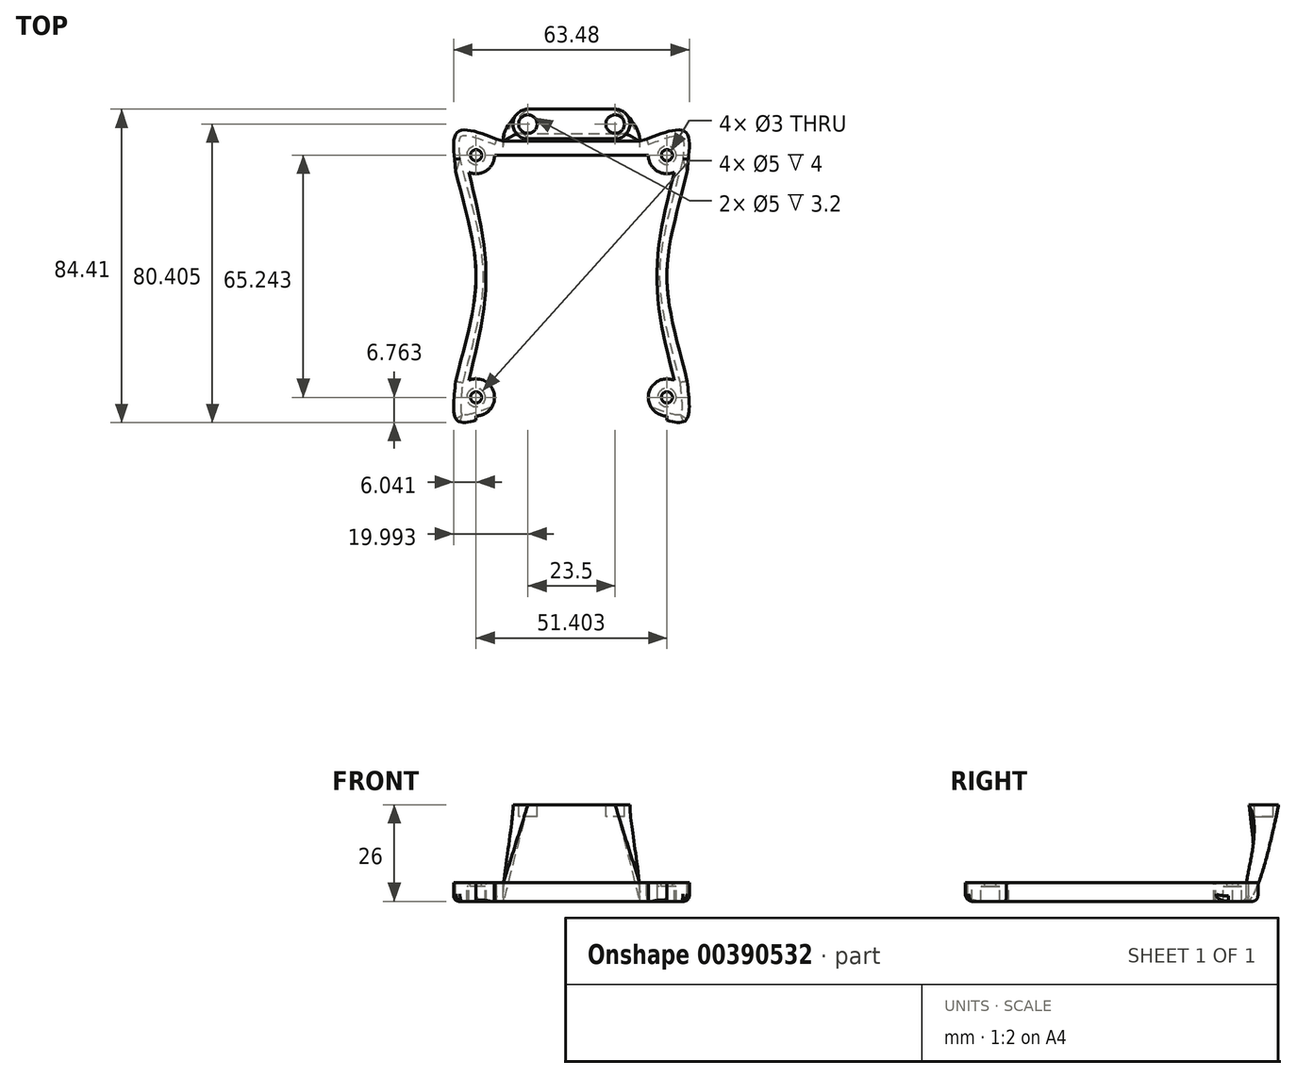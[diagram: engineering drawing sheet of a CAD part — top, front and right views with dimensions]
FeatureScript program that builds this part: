
annotation { "Feature Type Name" : "Feature", "Feature Type Description" : "" }
export const myFeature = defineFeature(function(context is Context, id is Id, definition is map)
    precondition{}
    {
        {
            var Q0;
            Q0=qCreatedBy(makeId("Top.planeOp"),FACE);
            var sketch = newSketch(context, id + "F0", { "sketchPlane" : qUnion([Q0])});
            skPoint(sketch, "E0.middle", {"position": v(-2.33, 0.15) * mm});
            skLineSegment(sketch, "E1.bottom", {"start": v(23.37, 32.78) * mm, "end": v(-28.03, 32.78) * mm, "construction": true});
            skLineSegment(sketch, "E1.top", {"start": v(23.37, -32.47) * mm, "end": v(-28.03, -32.47) * mm, "construction": true});
            skLineSegment(sketch, "E1.left", {"start": v(23.37, 32.78) * mm, "end": v(23.37, -32.47) * mm, "construction": true});
            skLineSegment(sketch, "E1.right", {"start": v(-28.03, 32.78) * mm, "end": v(-28.03, -32.47) * mm, "construction": true});
            skLineSegment(sketch, "E2.bottom", {"start": v(-67.33, 82.65) * mm, "end": v(62.67, 82.65) * mm, "construction": true});
            skLineSegment(sketch, "E2.top", {"start": v(-67.33, -82.35) * mm, "end": v(62.67, -82.35) * mm, "construction": true});
            skLineSegment(sketch, "E2.left", {"start": v(-67.33, 82.65) * mm, "end": v(-67.33, -82.35) * mm, "construction": true});
            skLineSegment(sketch, "E2.right", {"start": v(62.67, 82.65) * mm, "end": v(62.67, -82.35) * mm, "construction": true});
            skCircle(sketch, "E3", {"center": v(62.67, 82.65) * mm, "radius": 4.5 * mm, "construction": true});
            skCircle(sketch, "E4", {"center": v(-67.33, 82.65) * mm, "radius": 4.5 * mm, "construction": true});
            skCircle(sketch, "E5", {"center": v(62.67, -82.35) * mm, "radius": 4.5 * mm, "construction": true});
            skCircle(sketch, "E6", {"center": v(-67.33, -82.35) * mm, "radius": 4.5 * mm, "construction": true});
            skCircle(sketch, "E7", {"center": v(62.67, 82.65) * mm, "radius": 8 * mm, "construction": true});
            skCircle(sketch, "E8", {"center": v(62.67, -82.35) * mm, "radius": 8 * mm, "construction": true});
            skCircle(sketch, "E9", {"center": v(-67.33, -82.35) * mm, "radius": 8 * mm, "construction": true});
            skCircle(sketch, "E10", {"center": v(-67.33, 82.65) * mm, "radius": 8 * mm, "construction": true});
            skCircle(sketch, "E11", {"center": v(62.67, 82.65) * mm, "radius": 9.5 * mm, "construction": true});
            skCircle(sketch, "E12", {"center": v(62.67, -82.35) * mm, "radius": 9.5 * mm, "construction": true});
            skCircle(sketch, "E13", {"center": v(-67.33, -82.35) * mm, "radius": 9.5 * mm, "construction": true});
            skCircle(sketch, "E14", {"center": v(-67.33, 82.65) * mm, "radius": 9.5 * mm, "construction": true});
            skCircle(sketch, "E15", {"center": v(62.67, 82.65) * mm, "radius": 14 * mm, "construction": true});
            skCircle(sketch, "E16", {"center": v(-67.33, 82.65) * mm, "radius": 14 * mm, "construction": true});
            skCircle(sketch, "E17", {"center": v(62.67, -82.35) * mm, "radius": 14 * mm, "construction": true});
            skCircle(sketch, "E18", {"center": v(-67.33, -82.35) * mm, "radius": 14 * mm, "construction": true});
            skCircle(sketch, "E19", {"center": v(62.67, 82.65) * mm, "radius": 63.5 * mm, "construction": true});
            skCircle(sketch, "E20", {"center": v(62.67, -82.35) * mm, "radius": 63.5 * mm, "construction": true});
            skCircle(sketch, "E21", {"center": v(-67.33, -82.35) * mm, "radius": 63.5 * mm, "construction": true});
            skCircle(sketch, "E22", {"center": v(-67.33, 82.65) * mm, "radius": 63.5 * mm, "construction": true});
            skLineSegment(sketch, "E23.bottom", {"start": v(-28.52, 26.34) * mm, "end": v(23.86, 26.34) * mm, "construction": true});
            skLineSegment(sketch, "E23.top", {"start": v(-28.52, -26.04) * mm, "end": v(23.86, -26.04) * mm, "construction": true});
            skLineSegment(sketch, "E23.left", {"start": v(-28.52, 26.34) * mm, "end": v(-28.52, -26.04) * mm, "construction": true});
            skLineSegment(sketch, "E23.right", {"start": v(23.86, 26.34) * mm, "end": v(23.86, -26.04) * mm, "construction": true});
            skCircle(sketch, "E24", {"center": v(23.37, 32.78) * mm, "radius": 1.5 * mm, "construction": true});
            skCircle(sketch, "E25", {"center": v(-28.03, 32.78) * mm, "radius": 1.5 * mm, "construction": true});
            skCircle(sketch, "E26", {"center": v(23.37, -32.47) * mm, "radius": 1.5 * mm, "construction": true});
            skCircle(sketch, "E27", {"center": v(-28.03, -32.47) * mm, "radius": 1.5 * mm, "construction": true});
            skLineSegment(sketch, "E28", {"start": v(-67.33, 82.65) * mm, "end": v(62.67, -82.35) * mm, "construction": true});
            skLineSegment(sketch, "E29", {"start": v(62.67, 82.65) * mm, "end": v(-67.33, -82.35) * mm, "construction": true});
            skLineSegment(sketch, "E30.bottom", {"start": v(-17.58, -3.46) * mm, "end": v(12.92, -3.46) * mm, "construction": true});
            skLineSegment(sketch, "E30.top", {"start": v(-17.58, -33.96) * mm, "end": v(12.92, -33.96) * mm, "construction": true});
            skLineSegment(sketch, "E30.left", {"start": v(-17.58, -3.46) * mm, "end": v(-17.58, -33.96) * mm, "construction": true});
            skLineSegment(sketch, "E30.right", {"start": v(12.92, -3.46) * mm, "end": v(12.92, -33.96) * mm, "construction": true});
            skPoint(sketch, "E30.middle", {"position": v(-2.33, -18.71) * mm});
            skLineSegment(sketch, "E31.bottom", {"start": v(-17.58, 33.04) * mm, "end": v(12.92, 33.04) * mm, "construction": true});
            skLineSegment(sketch, "E31.top", {"start": v(-17.58, 2.54) * mm, "end": v(12.92, 2.54) * mm, "construction": true});
            skLineSegment(sketch, "E31.left", {"start": v(-17.58, 33.04) * mm, "end": v(-17.58, 2.54) * mm, "construction": true});
            skLineSegment(sketch, "E31.right", {"start": v(12.92, 33.04) * mm, "end": v(12.92, 2.54) * mm, "construction": true});
            skPoint(sketch, "E31.middle", {"position": v(-2.33, 17.79) * mm});
            skLineSegment(sketch, "E32", {"start": v(-2.33, 2.54) * mm, "end": v(-2.33, -3.46) * mm, "construction": true});
            skLineSegment(sketch, "E33", {"start": v(-2.33, 41.17) * mm, "end": v(-14.08, 41.17) * mm, "construction": true});
            skLineSegment(sketch, "E34", {"start": v(-2.33, 41.17) * mm, "end": v(9.42, 41.17) * mm, "construction": true});
            skLineSegment(sketch, "E35", {"start": v(-28.03, 32.78) * mm, "end": v(-22.53, 37.1) * mm, "construction": true});
            skLineSegment(sketch, "E36", {"start": v(-28.03, 32.78) * mm, "end": v(-33.53, 28.44) * mm, "construction": true});
            skLineSegment(sketch, "E37", {"start": v(-28.03, 32.78) * mm, "end": v(-32.98, 39.06) * mm, "construction": true});
            skLineSegment(sketch, "E38", {"start": v(23.37, 32.78) * mm, "end": v(28.33, 39.06) * mm, "construction": true});
            skLineSegment(sketch, "E39", {"start": v(23.37, 32.78) * mm, "end": v(17.88, 37.1) * mm, "construction": true});
            skLineSegment(sketch, "E40", {"start": v(23.37, 32.78) * mm, "end": v(28.87, 28.44) * mm, "construction": true});
            skLineSegment(sketch, "E41", {"start": v(23.37, -32.47) * mm, "end": v(28.33, -38.75) * mm, "construction": true});
            skLineSegment(sketch, "E42", {"start": v(23.37, -32.47) * mm, "end": v(17.88, -36.8) * mm, "construction": true});
            skLineSegment(sketch, "E43", {"start": v(23.37, -32.47) * mm, "end": v(28.87, -28.13) * mm, "construction": true});
            skLineSegment(sketch, "E44", {"start": v(-28.03, -32.47) * mm, "end": v(-32.98, -38.75) * mm, "construction": true});
            skLineSegment(sketch, "E45", {"start": v(-28.03, -32.47) * mm, "end": v(-22.53, -36.8) * mm, "construction": true});
            skLineSegment(sketch, "E46", {"start": v(-28.03, -32.47) * mm, "end": v(-33.53, -28.13) * mm, "construction": true});
            skFitSpline(sketch, "E47", {"points": [v(-22.53, 37.1) * mm, v(-32.98, 39.06) * mm, v(-33.53, 28.44) * mm], "startDerivative": vector(-20.3, 7.46) * mm, "endDerivative": vector(0.93, -21.61) * mm});
            skFitSpline(sketch, "E48", {"points": [v(17.88, 37.1) * mm, v(28.33, 39.06) * mm, v(28.87, 28.44) * mm], "startDerivative": vector(20.3, 7.46) * mm, "endDerivative": vector(-0.93, -21.61) * mm});
            skLineSegment(sketch, "E49", {"start": v(-14.08, 41.17) * mm, "end": v(-18.08, 41.17) * mm, "construction": true});
            skLineSegment(sketch, "E50", {"start": v(9.42, 41.17) * mm, "end": v(13.42, 41.17) * mm, "construction": true});
            skLineSegment(sketch, "E51", {"start": v(-2.33, 41.17) * mm, "end": v(-2.33, 45.17) * mm, "construction": true});
            skLineSegment(sketch, "E52", {"start": v(-18.08, 41.17) * mm, "end": v(-18.08, 41.17) * mm});
            skLineSegment(sketch, "E53", {"start": v(13.42, 41.17) * mm, "end": v(13.42, 41.17) * mm});
            skPoint(sketch, "E54.visualSharp", {"position": v(-18.08, 45.17) * mm});
            skPoint(sketch, "E55.visualSharp", {"position": v(13.42, 45.17) * mm});
            skLineSegment(sketch, "E56", {"start": v(-22.53, 37.1) * mm, "end": v(-20.66, 36.53) * mm});
            skPoint(sketch, "E57.visualSharp", {"position": v(-18.08, 35.74) * mm});
            skLineSegment(sketch, "E58", {"start": v(-18.08, 35.74) * mm, "end": v(-2.33, 35.74) * mm, "construction": true});
            skLineSegment(sketch, "E59", {"start": v(-2.33, 35.74) * mm, "end": v(13.42, 35.74) * mm, "construction": true});
            skLineSegment(sketch, "E60", {"start": v(17.88, 37.1) * mm, "end": v(16.01, 36.53) * mm});
            skPoint(sketch, "E61.visualSharp", {"position": v(13.42, 35.74) * mm});
            skCircle(sketch, "E62", {"center": v(-17.58, -33.96) * mm, "radius": 1.5 * mm});
            skCircle(sketch, "E63", {"center": v(12.92, -33.96) * mm, "radius": 1.5 * mm});
            skLineSegment(sketch, "E64", {"start": v(-2.33, -33.96) * mm, "end": v(-2.33, -37.96) * mm, "construction": true});
            skLineSegment(sketch, "E65", {"start": v(-17.58, -33.96) * mm, "end": v(-21.58, -33.96) * mm, "construction": true});
            skLineSegment(sketch, "E66", {"start": v(12.92, -33.96) * mm, "end": v(16.92, -33.96) * mm, "construction": true});
            skLineSegment(sketch, "E67", {"start": v(-21.58, -38.3) * mm, "end": v(-2.33, -38.3) * mm, "construction": true});
            skLineSegment(sketch, "E68", {"start": v(-2.33, -38.3) * mm, "end": v(16.92, -38.3) * mm, "construction": true});
            skPoint(sketch, "E69.visualSharp", {"position": v(-21.58, -38.3) * mm});
            skPoint(sketch, "E70.visualSharp", {"position": v(16.92, -38.3) * mm});
            skCircle(sketch, "E71", {"center": v(-12.13, -44.75) * mm, "radius": 1.5 * mm});
            skCircle(sketch, "E72", {"center": v(7.47, -44.75) * mm, "radius": 1.5 * mm});
            skLineSegment(sketch, "E73", {"start": v(-12.13, -44.75) * mm, "end": v(-2.33, -44.75) * mm, "construction": true});
            skLineSegment(sketch, "E74", {"start": v(-2.33, -44.75) * mm, "end": v(7.47, -44.75) * mm, "construction": true});
            skFitSpline(sketch, "E75", {"points": [v(-33.53, 28.44) * mm, v(-28.03, 0.15) * mm, v(-33.53, -28.13) * mm], "startDerivative": vector(16.96, -67.18) * mm, "endDerivative": vector(-16.96, -67.18) * mm});
            skFitSpline(sketch, "E76", {"points": [v(28.87, 28.44) * mm, v(23.37, 0.15) * mm, v(28.87, -28.13) * mm], "startDerivative": vector(-16.96, -67.18) * mm, "endDerivative": vector(16.96, -67.18) * mm});
            skLineSegment(sketch, "E77", {"start": v(-2.33, -44.75) * mm, "end": v(-2.33, -50.75) * mm, "construction": true});
            skLineSegment(sketch, "E78", {"start": v(-12.13, -44.75) * mm, "end": v(-16.13, -44.75) * mm, "construction": true});
            skLineSegment(sketch, "E79", {"start": v(-12.13, -44.75) * mm, "end": v(-12.13, -48.75) * mm, "construction": true});
            skLineSegment(sketch, "E80", {"start": v(7.47, -44.75) * mm, "end": v(11.47, -44.75) * mm, "construction": true});
            skLineSegment(sketch, "E81", {"start": v(7.47, -44.75) * mm, "end": v(7.47, -48.75) * mm, "construction": true});
            skCircle(sketch, "E82", {"center": v(-28.03, 32.78) * mm, "radius": 1.5 * mm});
            skCircle(sketch, "E83", {"center": v(23.37, 32.78) * mm, "radius": 1.5 * mm});
            skCircle(sketch, "E84", {"center": v(-28.03, -32.47) * mm, "radius": 1.5 * mm});
            skCircle(sketch, "E85", {"center": v(23.37, -32.47) * mm, "radius": 1.5 * mm});
            skLineSegment(sketch, "E86", {"start": v(-2.33, 32.78) * mm, "end": v(-2.33, 41.17) * mm, "construction": true});
            skLineSegment(sketch, "E87", {"start": v(115.22, -24.48) * mm, "end": v(115.22, 9.49) * mm, "construction": true});
            skLineSegment(sketch, "E88", {"start": v(-21.37, -36.36) * mm, "end": v(-2.33, -36.36) * mm, "construction": true});
            skLineSegment(sketch, "E89", {"start": v(-2.33, -36.36) * mm, "end": v(16.72, -36.36) * mm, "construction": true});
            skFitSpline(sketch, "E90", {"points": [v(-21.58, -38.3) * mm, v(-16.13, -44.75) * mm, v(-12.13, -48.75) * mm, v(-2.33, -50.75) * mm], "startDerivative": vector(17.01, -18.5) * mm, "endDerivative": vector(29.8, -3.11) * mm});
            skFitSpline(sketch, "E91", {"points": [v(16.92, -38.3) * mm, v(11.47, -44.75) * mm, v(7.47, -48.75) * mm, v(-2.33, -50.75) * mm], "startDerivative": vector(-17.98, -19.6) * mm, "endDerivative": vector(-29.8, -3.11) * mm});
            skLineSegment(sketch, "E92", {"start": v(116.25, 10.49) * mm, "end": v(169.47, 8.84) * mm, "construction": true});
            skPoint(sketch, "E93.visualSharp", {"position": v(115.22, 10.52) * mm});
            skArc(sketch, "E93.filletArc", {"start": v(116.25, 10.49) * mm, "mid": v(115.53, 10.2) * mm, "end": v(115.22, 9.49) * mm, "construction": true});
            skPoint(sketch, "E94.visualSharp", {"position": v(16.72, -36.36) * mm});
            skPoint(sketch, "E95.visualSharp", {"position": v(-21.37, -36.36) * mm});
            skLineSegment(sketch, "E96.bottom", {"start": v(-16.1, 17.65) * mm, "end": v(11.45, 17.65) * mm, "construction": true});
            skLineSegment(sketch, "E96.top", {"start": v(-16.1, -17.35) * mm, "end": v(11.45, -17.35) * mm, "construction": true});
            skLineSegment(sketch, "E96.left", {"start": v(-16.1, 17.65) * mm, "end": v(-16.1, -17.35) * mm, "construction": true});
            skLineSegment(sketch, "E96.right", {"start": v(11.45, 17.65) * mm, "end": v(11.45, -17.35) * mm, "construction": true});
            skLineSegment(sketch, "E97", {"start": v(-2.33, 13.23) * mm, "end": v(-20.53, 13.23) * mm, "construction": true});
            skLineSegment(sketch, "E98", {"start": v(-2.33, 13.23) * mm, "end": v(15.88, 13.23) * mm, "construction": true});
            skLineSegment(sketch, "E99", {"start": v(-2.33, 0.15) * mm, "end": v(-2.33, 14.42) * mm, "construction": true});
            skLineSegment(sketch, "E100", {"start": v(-2.33, 0.15) * mm, "end": v(14.67, 0.15) * mm, "construction": true});
            skLineSegment(sketch, "E101.bottom", {"start": v(-18.22, 14.7) * mm, "end": v(13.57, 14.7) * mm, "construction": true});
            skLineSegment(sketch, "E101.top", {"start": v(-18.22, -14.4) * mm, "end": v(13.57, -14.4) * mm, "construction": true});
            skLineSegment(sketch, "E101.left", {"start": v(-18.22, 14.7) * mm, "end": v(-18.22, -14.4) * mm, "construction": true});
            skLineSegment(sketch, "E101.right", {"start": v(13.57, 14.7) * mm, "end": v(13.57, -14.4) * mm, "construction": true});
            skLineSegment(sketch, "E102", {"start": v(-2.33, 26.07) * mm, "end": v(12, 26.07) * mm, "construction": true});
            skLineSegment(sketch, "E103", {"start": v(-2.33, 26.07) * mm, "end": v(-16.66, 26.07) * mm, "construction": true});
            skLineSegment(sketch, "E104.top", {"start": v(-17.4, 22.07) * mm, "end": v(-15.9, 22.07) * mm});
            skPoint(sketch, "E104.middle", {"position": v(-16.66, 26.07) * mm});
            skLineSegment(sketch, "E105.top", {"start": v(12.75, 22.07) * mm, "end": v(11.25, 22.07) * mm});
            skLineSegment(sketch, "E105.left", {"start": v(12.75, 30.07) * mm, "end": v(12.75, 22.07) * mm});
            skPoint(sketch, "E105.middle", {"position": v(12, 26.07) * mm});
            skFitSpline(sketch, "E106", {"points": [v(-33.53, -28.13) * mm, v(-32.98, -38.75) * mm, v(-22.93, -36.94) * mm], "startDerivative": vector(-1.92, -24.87) * mm, "endDerivative": vector(23.17, 7.34) * mm});
            skLineSegment(sketch, "E107", {"start": v(-22.93, -36.94) * mm, "end": v(-2.33, -36.94) * mm, "construction": true});
            skLineSegment(sketch, "E108", {"start": v(-2.33, -36.94) * mm, "end": v(18.28, -36.94) * mm, "construction": true});
            skLineSegment(sketch, "E109", {"start": v(16.92, -38.3) * mm, "end": v(17.66, -37.14) * mm});
            skLineSegment(sketch, "E110", {"start": v(18.25, -36.93) * mm, "end": v(18.28, -36.94) * mm});
            skLineSegment(sketch, "E111", {"start": v(-21.58, -38.3) * mm, "end": v(-22.32, -37.14) * mm});
            skLineSegment(sketch, "E112", {"start": v(-22.9, -36.93) * mm, "end": v(-22.93, -36.94) * mm});
            skLineSegment(sketch, "E113", {"start": v(169.47, 8.84) * mm, "end": v(169.47, -13.62) * mm, "construction": true});
            skPoint(sketch, "E114.visualSharp", {"position": v(17.88, -36.8) * mm});
            skArc(sketch, "E114.filletArc", {"start": v(18.25, -36.93) * mm, "mid": v(17.92, -36.93) * mm, "end": v(17.66, -37.14) * mm});
            skPoint(sketch, "E115.visualSharp", {"position": v(-22.53, -36.8) * mm});
            skArc(sketch, "E115.filletArc", {"start": v(-22.32, -37.14) * mm, "mid": v(-22.58, -36.93) * mm, "end": v(-22.9, -36.93) * mm});
            skLineSegment(sketch, "E116", {"start": v(-2.33, 0.15) * mm, "end": v(-2.33, 3.45) * mm, "construction": true});
            skLineSegment(sketch, "E117.bottom", {"start": v(-7.83, 5.65) * mm, "end": v(3.17, 5.65) * mm, "construction": true});
            skLineSegment(sketch, "E117.top", {"start": v(-7.83, -5.35) * mm, "end": v(3.17, -5.35) * mm, "construction": true});
            skLineSegment(sketch, "E117.left", {"start": v(-7.83, 5.65) * mm, "end": v(-7.83, -5.35) * mm, "construction": true});
            skLineSegment(sketch, "E117.right", {"start": v(3.17, 5.65) * mm, "end": v(3.17, -5.35) * mm, "construction": true});
            skLineSegment(sketch, "E118.bottom", {"start": v(-10.3, 10.77) * mm, "end": v(5.65, 10.77) * mm});
            skPoint(sketch, "E118.middle", {"position": v(-2.33, 12.75) * mm});
            skPoint(sketch, "E119.middle", {"position": v(-2.33, -26.45) * mm});
            skPoint(sketch, "E120", {"position": v(-2.33, -17.35) * mm});
            skPoint(sketch, "E121", {"position": v(-2.33, -26.04) * mm});
            skPoint(sketch, "E122.visualSharp", {"position": v(-2.33, 21.17) * mm});
            skArc(sketch, "E122.filletArc", {"start": v(-0.91, 19.76) * mm, "mid": v(-2.33, 20.34) * mm, "end": v(-3.74, 19.76) * mm});
            skPoint(sketch, "E123.visualSharp", {"position": v(-12.72, 10.77) * mm});
            skArc(sketch, "E123.filletArc", {"start": v(-11.02, 12.48) * mm, "mid": v(-11.23, 11.4) * mm, "end": v(-10.3, 10.77) * mm});
            skPoint(sketch, "E124.visualSharp", {"position": v(8.07, 10.77) * mm});
            skArc(sketch, "E124.filletArc", {"start": v(5.65, 10.77) * mm, "mid": v(6.58, 11.4) * mm, "end": v(6.36, 12.48) * mm});
            skPoint(sketch, "E125.visualSharp", {"position": v(-2.33, 0.75) * mm});
            skLineSegment(sketch, "E126", {"start": v(-1.33, 10.77) * mm, "end": v(-1.33, 6.27) * mm, "construction": true});
            skPoint(sketch, "E127.middle", {"position": v(-2.33, 9.75) * mm});
            skCircle(sketch, "E128", {"center": v(13.57, 14.7) * mm, "radius": 4.5 * mm, "construction": true});
            skCircle(sketch, "E129", {"center": v(-18.22, 14.7) * mm, "radius": 4.5 * mm, "construction": true});
            skCircle(sketch, "E130", {"center": v(13.57, -14.4) * mm, "radius": 4.5 * mm, "construction": true});
            skCircle(sketch, "E131", {"center": v(-18.22, -14.4) * mm, "radius": 4.5 * mm, "construction": true});
            skLineSegment(sketch, "E132", {"start": v(-2.33, 0.15) * mm, "end": v(-18.22, 14.7) * mm, "construction": true});
            skLineSegment(sketch, "E133", {"start": v(-2.33, 0.15) * mm, "end": v(13.57, 14.7) * mm, "construction": true});
            skLineSegment(sketch, "E134", {"start": v(13.57, 14.7) * mm, "end": v(23.37, 32.78) * mm, "construction": true});
            skLineSegment(sketch, "E135", {"start": v(-18.22, 14.7) * mm, "end": v(-28.03, 32.78) * mm, "construction": true});
            skLineSegment(sketch, "E136", {"start": v(-2.33, 0.15) * mm, "end": v(-18.22, -14.4) * mm, "construction": true});
            skLineSegment(sketch, "E137", {"start": v(-18.22, -14.4) * mm, "end": v(-28.03, -32.47) * mm, "construction": true});
            skLineSegment(sketch, "E138", {"start": v(-2.33, 0.15) * mm, "end": v(13.57, -14.4) * mm, "construction": true});
            skLineSegment(sketch, "E139", {"start": v(13.57, -14.4) * mm, "end": v(23.37, -32.47) * mm, "construction": true});
            skPoint(sketch, "E140.visualSharp", {"position": v(-4.57, 37.81) * mm});
            skPoint(sketch, "E141.visualSharp", {"position": v(-12.93, 29.46) * mm});
            skPoint(sketch, "E142.visualSharp", {"position": v(-4.57, 26.22) * mm});
            skArc(sketch, "E142.filletArc", {"start": v(-5.16, 25.63) * mm, "mid": v(-4.73, 26.28) * mm, "end": v(-4.57, 27.04) * mm});
            skPoint(sketch, "E143.visualSharp", {"position": v(-0.08, 26.22) * mm});
            skPoint(sketch, "E144.visualSharp", {"position": v(-0.08, 37.81) * mm});
            skPoint(sketch, "E145.visualSharp", {"position": v(8.28, 17.86) * mm});
            skPoint(sketch, "E146.visualSharp", {"position": v(-12.93, 17.86) * mm});
            skLineSegment(sketch, "E147", {"start": v(-2.33, -22.87) * mm, "end": v(-10.31, -22.87) * mm});
            skLineSegment(sketch, "E148", {"start": v(-2.33, -22.87) * mm, "end": v(5.66, -22.87) * mm});
            skPoint(sketch, "E149.visualSharp", {"position": v(8.07, -22.87) * mm});
            skArc(sketch, "E149.filletArc", {"start": v(6.37, -24.57) * mm, "mid": v(6.58, -23.48) * mm, "end": v(5.66, -22.87) * mm});
            skPoint(sketch, "E150.visualSharp", {"position": v(-12.73, -22.87) * mm});
            skArc(sketch, "E150.filletArc", {"start": v(-10.31, -22.87) * mm, "mid": v(-11.24, -23.48) * mm, "end": v(-11.02, -24.57) * mm});
            skPoint(sketch, "E151.visualSharp", {"position": v(-2.33, -33.27) * mm});
            skArc(sketch, "E151.filletArc", {"start": v(-3.74, -31.85) * mm, "mid": v(-2.33, -32.44) * mm, "end": v(-0.91, -31.85) * mm});
            skFitSpline(sketch, "E152", {"points": [v(28.87, -28.13) * mm, v(28.33, -38.75) * mm, v(18.28, -36.94) * mm], "startDerivative": vector(1.93, -24.89) * mm, "endDerivative": vector(-23.2, 7.39) * mm});
            skLineSegment(sketch, "E153", {"start": v(-5.66, -36.7) * mm, "end": v(-5.66, -42.34) * mm});
            skLineSegment(sketch, "E154", {"start": v(-12.73, -36.85) * mm, "end": v(-12.73, -31.22) * mm});
            skLineSegment(sketch, "E155", {"start": v(1, -36.7) * mm, "end": v(1, -42.34) * mm});
            skLineSegment(sketch, "E156", {"start": v(8.07, -36.85) * mm, "end": v(8.07, -31.22) * mm});
            skPoint(sketch, "E157.visualSharp", {"position": v(8.07, -28.8) * mm});
            skArc(sketch, "E157.filletArc", {"start": v(8.07, -31.22) * mm, "mid": v(7.46, -30.3) * mm, "end": v(6.37, -30.5) * mm});
            skPoint(sketch, "E158.visualSharp", {"position": v(1, -44.75) * mm});
            skArc(sketch, "E158.filletArc", {"start": v(1, -42.34) * mm, "mid": v(1.62, -43.26) * mm, "end": v(2.7, -43.05) * mm});
            skPoint(sketch, "E159.visualSharp", {"position": v(-5.66, -44.75) * mm});
            skArc(sketch, "E159.filletArc", {"start": v(-7.36, -43.05) * mm, "mid": v(-6.27, -43.26) * mm, "end": v(-5.66, -42.34) * mm});
            skPoint(sketch, "E160.visualSharp", {"position": v(-12.73, -28.8) * mm});
            skArc(sketch, "E160.filletArc", {"start": v(-11.02, -30.5) * mm, "mid": v(-12.1, -30.3) * mm, "end": v(-12.73, -31.22) * mm});
            skPoint(sketch, "E161.visualSharp", {"position": v(-5.66, -35.87) * mm});
            skArc(sketch, "E161.filletArc", {"start": v(-5.66, -36.7) * mm, "mid": v(-5.8, -35.94) * mm, "end": v(-6.24, -35.29) * mm});
            skPoint(sketch, "E162.visualSharp", {"position": v(-12.73, -37.68) * mm});
            skArc(sketch, "E162.filletArc", {"start": v(-12.73, -36.85) * mm, "mid": v(-12.57, -37.62) * mm, "end": v(-12.14, -38.27) * mm});
            skPoint(sketch, "E163.visualSharp", {"position": v(1, -35.87) * mm});
            skArc(sketch, "E163.filletArc", {"start": v(1.59, -35.29) * mm, "mid": v(1.15, -35.94) * mm, "end": v(1, -36.7) * mm});
            skPoint(sketch, "E164.visualSharp", {"position": v(8.07, -37.68) * mm});
            skArc(sketch, "E164.filletArc", {"start": v(7.49, -38.27) * mm, "mid": v(7.92, -37.62) * mm, "end": v(8.07, -36.85) * mm});
            skLineSegment(sketch, "E165", {"start": v(-2.33, -18.71) * mm, "end": v(-10.31, -18.71) * mm});
            skLineSegment(sketch, "E166", {"start": v(-2.33, -18.71) * mm, "end": v(5.66, -18.71) * mm});
            skPoint(sketch, "E167.visualSharp", {"position": v(-2.33, -8.31) * mm});
            skArc(sketch, "E167.filletArc", {"start": v(-0.91, -9.72) * mm, "mid": v(-2.33, -9.14) * mm, "end": v(-3.74, -9.72) * mm});
            skPoint(sketch, "E168.visualSharp", {"position": v(-12.73, -18.71) * mm});
            skArc(sketch, "E168.filletArc", {"start": v(-11.02, -17) * mm, "mid": v(-11.24, -18.1) * mm, "end": v(-10.31, -18.71) * mm});
            skPoint(sketch, "E169.visualSharp", {"position": v(8.07, -18.71) * mm});
            skArc(sketch, "E169.filletArc", {"start": v(5.66, -18.71) * mm, "mid": v(6.58, -18.1) * mm, "end": v(6.37, -17) * mm});
            skLineSegment(sketch, "E170", {"start": v(14.67, 0.15) * mm, "end": v(17.67, 0.15) * mm, "construction": true});
            skCircle(sketch, "E171", {"center": v(23.37, 32.78) * mm, "radius": 7 * mm, "construction": true});
            skLineSegment(sketch, "E172", {"start": v(17.64, 12.88) * mm, "end": v(21.69, 20.22) * mm});
            skLineSegment(sketch, "E173", {"start": v(16.8, 5.92) * mm, "end": v(12.23, 5.92) * mm});
            skPoint(sketch, "E174.visualSharp", {"position": v(22.7, 22.04) * mm});
            skArc(sketch, "E174.filletArc", {"start": v(22.15, 20.04) * mm, "mid": v(22, 20.33) * mm, "end": v(21.69, 20.22) * mm});
            skPoint(sketch, "E175.visualSharp", {"position": v(18.33, 5.92) * mm});
            skArc(sketch, "E175.filletArc", {"start": v(16.8, 5.92) * mm, "mid": v(18.02, 6.34) * mm, "end": v(18.73, 7.4) * mm});
            skPoint(sketch, "E176.visualSharp", {"position": v(9.29, 5.92) * mm});
            skArc(sketch, "E176.filletArc", {"start": v(11.62, 7.72) * mm, "mid": v(11.28, 6.6) * mm, "end": v(12.23, 5.92) * mm});
            skPoint(sketch, "E177.visualSharp", {"position": v(17.14, 11.97) * mm});
            skArc(sketch, "E177.filletArc", {"start": v(16.31, 11.33) * mm, "mid": v(17.06, 12.04) * mm, "end": v(17.64, 12.88) * mm});
            skLineSegment(sketch, "E178", {"start": v(9.29, 5.92) * mm, "end": v(-2.33, 5.92) * mm, "construction": true});
            skPoint(sketch, "E178.endSnap0", {"position": v(-2.33, 5.65) * mm});
            skLineSegment(sketch, "E179", {"start": v(-2.33, 5.92) * mm, "end": v(-13.94, 5.92) * mm, "construction": true});
            skLineSegment(sketch, "E180", {"start": v(-16.88, 5.92) * mm, "end": v(-21.46, 5.92) * mm});
            skLineSegment(sketch, "E181", {"start": v(17.14, 11.97) * mm, "end": v(-2.33, 11.97) * mm, "construction": true});
            skLineSegment(sketch, "E182", {"start": v(-2.33, 11.97) * mm, "end": v(-21.8, 11.97) * mm, "construction": true});
            skLineSegment(sketch, "E183", {"start": v(22.7, 22.04) * mm, "end": v(-2.33, 22.04) * mm, "construction": true});
            skLineSegment(sketch, "E184", {"start": v(-2.33, 22.04) * mm, "end": v(-27.34, 22.04) * mm, "construction": true});
            skLineSegment(sketch, "E185", {"start": v(-22.3, 12.88) * mm, "end": v(-26.34, 20.22) * mm});
            skPoint(sketch, "E186.visualSharp", {"position": v(-27.34, 22.04) * mm});
            skArc(sketch, "E186.filletArc", {"start": v(-26.34, 20.22) * mm, "mid": v(-26.65, 20.33) * mm, "end": v(-26.8, 20.04) * mm});
            skPoint(sketch, "E187.visualSharp", {"position": v(-13.94, 5.92) * mm});
            skArc(sketch, "E187.filletArc", {"start": v(-16.88, 5.92) * mm, "mid": v(-15.93, 6.6) * mm, "end": v(-16.27, 7.72) * mm});
            skPoint(sketch, "E188.visualSharp", {"position": v(-22.99, 5.92) * mm});
            skArc(sketch, "E188.filletArc", {"start": v(-23.39, 7.4) * mm, "mid": v(-22.67, 6.34) * mm, "end": v(-21.46, 5.92) * mm});
            skPoint(sketch, "E189.visualSharp", {"position": v(-21.8, 11.97) * mm});
            skArc(sketch, "E189.filletArc", {"start": v(-22.3, 12.88) * mm, "mid": v(-21.71, 12.04) * mm, "end": v(-20.97, 11.33) * mm});
            skLineSegment(sketch, "E190", {"start": v(-2.33, 43.17) * mm, "end": v(0, 43.17) * mm, "construction": true});
            skLineSegment(sketch, "E191", {"start": v(-20.66, 36.53) * mm, "end": v(16.01, 36.53) * mm});
            skSolve(sketch);
        }
        {
            var Q0;
            Q0=qCreatedBy(makeId("Top.planeOp"),FACE);
            cPlane(context, id + "F1", {"entities" : qUnion([Q0]), "cplaneType" : CPlaneType.OFFSET, "offset" : 21 * mm, "width" : 150 * mm, "height" : 150 * mm});
        }
        {
            var Q0;
            Q0=qCreatedBy(id+"F1.planeOp",FACE);
            var sketch = newSketch(context, id + "F2", { "sketchPlane" : qUnion([Q0])});
            skCircle(sketch, "E192", {"center": v(-14.08, 41.18) * mm, "radius": 4 * mm, "construction": true});
            skCircle(sketch, "E193", {"center": v(9.42, 41.18) * mm, "radius": 4 * mm, "construction": true});
            skLineSegment(sketch, "E194", {"start": v(-14.08, 41.18) * mm, "end": v(-14.08, 45.18) * mm, "construction": true});
            skLineSegment(sketch, "E195", {"start": v(-14.08, 41.18) * mm, "end": v(-18.08, 41.18) * mm, "construction": true});
            skLineSegment(sketch, "E196", {"start": v(9.42, 41.18) * mm, "end": v(9.42, 45.18) * mm, "construction": true});
            skLineSegment(sketch, "E197", {"start": v(9.42, 41.18) * mm, "end": v(13.42, 41.18) * mm, "construction": true});
            skArc(sketch, "E198", {"start": v(-14.08, 45.18) * mm, "mid": v(-16.9, 44) * mm, "end": v(-18.08, 41.18) * mm});
            skArc(sketch, "E199", {"start": v(13.42, 41.18) * mm, "mid": v(12.25, 44) * mm, "end": v(9.42, 45.18) * mm});
            skLineSegment(sketch, "E200", {"start": v(-14.08, 45.18) * mm, "end": v(9.42, 45.18) * mm});
            skLineSegment(sketch, "E201", {"start": v(-14.08, 41.18) * mm, "end": v(-14.08, 37.18) * mm, "construction": true});
            skLineSegment(sketch, "E202", {"start": v(9.42, 41.18) * mm, "end": v(9.42, 37.18) * mm, "construction": true});
            skArc(sketch, "E203", {"start": v(-18.08, 41.18) * mm, "mid": v(-16.9, 38.35) * mm, "end": v(-14.08, 37.18) * mm});
            skArc(sketch, "E204", {"start": v(9.42, 37.18) * mm, "mid": v(12.25, 38.35) * mm, "end": v(13.42, 41.18) * mm});
            skLineSegment(sketch, "E205", {"start": v(9.42, 37.18) * mm, "end": v(-14.08, 37.18) * mm});
            skLineSegment(sketch, "E206", {"start": v(-2.33, 37.18) * mm, "end": v(-2.33, 40.68) * mm, "construction": true});
            skLineSegment(sketch, "E207", {"start": v(-2.33, 40.68) * mm, "end": v(0, 40.68) * mm, "construction": true});
            skSolve(sketch);
        }
        {
            var Q0;
            Q0 = qSketchRegion(id + "F0", true);
            extrude(context, id + "F3", {"entities" : qUnion([Q0]), "oppositeDirection" : true, "depth" : 5 * mm});
        }
        {
            var Q0;
            Q0=sQuery(id+"F2.wireOp",VERTEX,"E200.start");
            var Q1;
            Q1=sQuery(id+"F2.wireOp",VERTEX,"E201.end");
            var Q2;
            Q2=makeQuery(id+"F3.opExtrude","CAP_VERTEX",VERTEX,{"disambiguationData":[OSD([sQuery(id+"F0.wireOp",EDGE,"E56"),sQuery(id+"F0.wireOp",EDGE,"E191")])],"isStart":true});
            cPlane(context, id + "F4", {"entities" : qUnion([Q0, Q1, Q2]), "cplaneType" : CPlaneType.THREE_POINT, "offset" : 25 * mm, "width" : 150 * mm, "height" : 150 * mm});
        }
        {
            var Q0;
            Q0=sQuery(id+"F2.wireOp",VERTEX,"E199.end");
            var Q1;
            Q1=sQuery(id+"F2.wireOp",VERTEX,"E205.start");
            var Q2;
            Q2=makeQuery(id+"F3.opExtrude","CAP_VERTEX",VERTEX,{"disambiguationData":[OSD([sQuery(id+"F0.wireOp",EDGE,"E60"),sQuery(id+"F0.wireOp",EDGE,"E191")])],"isStart":true});
            cPlane(context, id + "F5", {"entities" : qUnion([Q0, Q1, Q2]), "cplaneType" : CPlaneType.THREE_POINT, "offset" : 25 * mm, "width" : 150 * mm, "height" : 150 * mm});
        }
        {
            var Q0;
            Q0=qCreatedBy(id+"F4.planeOp",FACE);
            var sketch = newSketch(context, id + "F6", { "sketchPlane" : qUnion([Q0])});
            skFitSpline(sketch, "E208", {"points": [v(-37.18, 15.82) * mm, v(-36.53, -6.19) * mm], "startDerivative": vector(-8.46, -14.5) * mm, "endDerivative": vector(4.23, -21.62) * mm});
            skSolve(sketch);
        }
        {
            var Q0;
            Q0=sQuery(id+"F2.wireOp",VERTEX,"E200.start");
            var Q1;
            Q1=sQuery(id+"F6.wireOp",VERTEX,"E208.start");
            var Q2;
            Q2=makeQuery(id+"F3.opExtrude","CAP_VERTEX",VERTEX,{"disambiguationData":[OSD([sQuery(id+"F0.wireOp",EDGE,"E56"),sQuery(id+"F0.wireOp",EDGE,"E191")])],"isStart":false});
            cPlane(context, id + "F7", {"entities" : qUnion([Q0, Q1, Q2]), "cplaneType" : CPlaneType.THREE_POINT, "offset" : 25 * mm, "width" : 150 * mm, "height" : 150 * mm});
        }
        {
            var Q0;
            Q0=qCreatedBy(id+"F7.planeOp",FACE);
            var sketch = newSketch(context, id + "F8", { "sketchPlane" : qUnion([Q0])});
            skFitSpline(sketch, "E209", {"points": [v(-45.18, 16.9) * mm, v(-36.53, -9.92) * mm], "startDerivative": vector(1.94, -10.2) * mm, "endDerivative": vector(10.23, -0.3) * mm});
            skSolve(sketch);
        }
        {
            var Q0;
            Q0=qCreatedBy(id+"F5.planeOp",FACE);
            var sketch = newSketch(context, id + "F9", { "sketchPlane" : qUnion([Q0])});
            skFitSpline(sketch, "E210", {"points": [v(-37.18, 17.22) * mm, v(-36.53, -4.8) * mm], "startDerivative": vector(-9.48, -17.55) * mm, "endDerivative": vector(2.7, -19.83) * mm});
            skSolve(sketch);
        }
        {
            var Q0;
            Q0=sQuery(id+"F2.wireOp",VERTEX,"E199.end");
            var Q1;
            Q1=sQuery(id+"F9.wireOp",VERTEX,"E210.start");
            var Q2;
            Q2=makeQuery(id+"F3.opExtrude","CAP_VERTEX",VERTEX,{"disambiguationData":[OSD([sQuery(id+"F0.wireOp",EDGE,"E60"),sQuery(id+"F0.wireOp",EDGE,"E191")])],"isStart":false});
            cPlane(context, id + "F10", {"entities" : qUnion([Q0, Q1, Q2]), "cplaneType" : CPlaneType.THREE_POINT, "offset" : 25 * mm, "width" : 150 * mm, "height" : 150 * mm});
        }
        {
            var Q0;
            Q0=qCreatedBy(id+"F10.planeOp",FACE);
            var sketch = newSketch(context, id + "F11", { "sketchPlane" : qUnion([Q0])});
            skFitSpline(sketch, "E211", {"points": [v(-45.18, 18.04) * mm, v(-36.53, -8.78) * mm], "startDerivative": vector(1.66, -8.07) * mm, "endDerivative": vector(10.78, -0.87) * mm});
            skSolve(sketch);
        }
        {
            var Q1;
            Q1=makeQuery(id+"F2.imprint","IMPRINT",FACE,{"disambiguationData":[TD([[makeQuery(id+"F2.imprint","IMPRINT",EDGE,{"derivedFrom":sQuery(id+"F2.wireOp",EDGE,"E198")}),1.0]])]});
            var Q2;
            Q2=makeQuery(id+"F3.opExtrude","SWEPT_FACE",FACE,{"disambiguationData":[OSD([sQuery(id+"F0.wireOp",EDGE,"E191")])]});
            var Q3;
            Q3=sQuery(id+"F11.wireOp",EDGE,"E211");
            var Q4;
            Q4=sQuery(id+"F8.wireOp",EDGE,"E209");
            var Q5;
            Q5=sQuery(id+"F9.wireOp",EDGE,"E210");
            var Q6;
            Q6=sQuery(id+"F6.wireOp",EDGE,"E208");
            loft(context, id + "F12", {"operationType" : NewBodyOperationType.ADD, "addGuides" : true, "sheetProfilesArray" : [{ "sheetProfileEntities" : qUnion([Q1]) }, { "sheetProfileEntities" : qUnion([Q2]) }], "guidesArray" : [{ "guideEntities" : qUnion([Q3]), "guideDerivativeType" : LoftGuideDerivativeType.DEFAULT, "guideDerivativeMagnitude" : 1 }, { "guideEntities" : qUnion([Q4]), "guideDerivativeType" : LoftGuideDerivativeType.DEFAULT, "guideDerivativeMagnitude" : 1 }, { "guideEntities" : qUnion([Q5]), "guideDerivativeType" : LoftGuideDerivativeType.DEFAULT, "guideDerivativeMagnitude" : 1 }, { "guideEntities" : qUnion([Q6]), "guideDerivativeType" : LoftGuideDerivativeType.DEFAULT, "guideDerivativeMagnitude" : 1 }]});
        }
        {
            var Q0;
            Q0=qCreatedBy(makeId("Top.planeOp"),FACE);
            var sketch = newSketch(context, id + "F13", { "sketchPlane" : qUnion([Q0])});
            skLineSegment(sketch, "E212", {"start": v(0, 15.53) * mm, "end": v(-2.33, 15.53) * mm, "construction": true});
            skLineSegment(sketch, "E213", {"start": v(-2.33, 34.2) * mm, "end": v(-2.33, -48.18) * mm, "construction": true});
            skCircle(sketch, "E214", {"center": v(-28.03, 32.78) * mm, "radius": 5 * mm, "construction": true});
            skCircle(sketch, "E215", {"center": v(23.37, 32.78) * mm, "radius": 5 * mm, "construction": true});
            skLineSegment(sketch, "E216", {"start": v(-23.03, 32.78) * mm, "end": v(18.37, 32.78) * mm});
            skArc(sketch, "E217", {"start": v(-28.03, 27.78) * mm, "mid": v(-24.5, 29.24) * mm, "end": v(-23.03, 32.78) * mm});
            skArc(sketch, "E218", {"start": v(18.37, 32.78) * mm, "mid": v(19.84, 29.24) * mm, "end": v(23.37, 27.78) * mm});
            skCircle(sketch, "E219", {"center": v(-28.03, -32.47) * mm, "radius": 5 * mm, "construction": true});
            skCircle(sketch, "E220", {"center": v(23.37, -32.47) * mm, "radius": 5 * mm, "construction": true});
            skLineSegment(sketch, "E221", {"start": v(23.37, -37.47) * mm, "end": v(23.37, -52.19) * mm});
            skLineSegment(sketch, "E222", {"start": v(-2.33, 0) * mm, "end": v(-25.33, 0) * mm, "construction": true});
            skLineSegment(sketch, "E223", {"start": v(-2.33, 0) * mm, "end": v(20.67, 0) * mm, "construction": true});
            skArc(sketch, "E224", {"start": v(23.37, -27.47) * mm, "mid": v(18.37, -32.47) * mm, "end": v(23.37, -37.47) * mm});
            skLineSegment(sketch, "E225", {"start": v(-28.03, -37.47) * mm, "end": v(-28.03, -52.19) * mm});
            skLineSegment(sketch, "E226", {"start": v(-28.03, -52.19) * mm, "end": v(23.37, -52.19) * mm});
            skArc(sketch, "E227", {"start": v(-28.03, -37.47) * mm, "mid": v(-23.06, -32.47) * mm, "end": v(-28.03, -27.47) * mm});
            skLineSegment(sketch, "E228", {"start": v(-23.03, 32.78) * mm, "end": v(-30, 32.78) * mm, "construction": true});
            skLineSegment(sketch, "E229", {"start": v(18.37, 32.78) * mm, "end": v(25.35, 32.78) * mm, "construction": true});
            skLineSegment(sketch, "E230", {"start": v(-23.06, -32.47) * mm, "end": v(-30.03, -32.47) * mm, "construction": true});
            skLineSegment(sketch, "E231", {"start": v(18.37, -32.47) * mm, "end": v(25.35, -32.47) * mm, "construction": true});
            skPoint(sketch, "E231.startSnap0", {"position": v(18.37, -32.47) * mm});
            skFitSpline(sketch, "E232", {"points": [v(-30, 28.18) * mm, v(-25.33, 0) * mm, v(-30, -27.87) * mm], "startDerivative": vector(14.01, -56.3) * mm, "endDerivative": vector(-14.04, -55.82) * mm});
            skFitSpline(sketch, "E233", {"points": [v(25.35, 28.18) * mm, v(20.67, 0) * mm, v(25.35, -27.87) * mm], "startDerivative": vector(-14.01, -56.3) * mm, "endDerivative": vector(14.04, -55.82) * mm});
            skArc(sketch, "E234", {"start": v(-28.03, -27.47) * mm, "mid": v(-29.04, -27.57) * mm, "end": v(-30, -27.87) * mm});
            skArc(sketch, "E235", {"start": v(25.35, -27.87) * mm, "mid": v(24.38, -27.57) * mm, "end": v(23.37, -27.47) * mm});
            skArc(sketch, "E236", {"start": v(-30, 28.18) * mm, "mid": v(-29.04, 27.88) * mm, "end": v(-28.03, 27.78) * mm});
            skArc(sketch, "E237", {"start": v(23.37, 27.78) * mm, "mid": v(24.38, 27.88) * mm, "end": v(25.35, 28.18) * mm});
            skSolve(sketch);
        }
        {
            var Q0;
            Q0 = qSketchRegion(id + "F13", true);
            extrude(context, id + "F14", {"entities" : qUnion([Q0]), "operationType" : NewBodyOperationType.REMOVE, "oppositeDirection" : true, "depth" : 5 * mm});
        }
        {
            var Q0;
            Q0=makeQuery(id+"F3.opExtrude","CAP_EDGE",EDGE,{"disambiguationData":[OSD([sQuery(id+"F0.wireOp",EDGE,"E75")])],"isStart":false});
            var Q1;
            Q1=makeQuery(id+"F3.opExtrude","CAP_EDGE",EDGE,{"disambiguationData":[OSD([sQuery(id+"F0.wireOp",EDGE,"E76")])],"isStart":false});
            var Q2;
            Q2=makeQuery(id+"F14.boolean.opBoolean","COPY",EDGE,{"derivedFrom":makeQuery(id+"F14.opExtrude","CAP_EDGE",EDGE,{"disambiguationData":[OSD([sQuery(id+"F13.wireOp",EDGE,"3efa2638-28cb-410d-a451-7c4a5f4f91e7")])],"isStart":false})});
            var Q3;
            Q3=makeQuery(id+"F14.boolean.opBoolean","COPY",EDGE,{"derivedFrom":makeQuery(id+"F14.opExtrude","CAP_EDGE",EDGE,{"disambiguationData":[OSD([sQuery(id+"F13.wireOp",EDGE,"fab21a03-1c0a-4784-8c2c-017c8e7d5961")])],"isStart":false})});
            var Q4;
            Q4=makeQuery(id+"F3.opExtrude","CAP_EDGE",EDGE,{"disambiguationData":[OSD([sQuery(id+"F0.wireOp",EDGE,"E152")])],"isStart":false});
            var Q5;
            Q5=makeQuery(id+"F3.opExtrude","CAP_EDGE",EDGE,{"disambiguationData":[OSD([sQuery(id+"F0.wireOp",EDGE,"E106")])],"isStart":false});
            fillet(context, id + "F15", {"entities" : qUnion([Q0, Q1, Q2, Q3, Q4, Q5]), "radius" : 2 * mm, "tangentPropagation" : true, "allowEdgeOverflow" : false});
        }
        {
            var Q0;
            Q0=makeQuery(id+"F3.opExtrude","CAP_EDGE",EDGE,{"disambiguationData":[OSD([sQuery(id+"F0.wireOp",EDGE,"E47")])],"isStart":false});
            var Q1;
            Q1=makeQuery(id+"F3.opExtrude","CAP_EDGE",EDGE,{"disambiguationData":[OSD([sQuery(id+"F0.wireOp",EDGE,"E48")])],"isStart":false});
            fillet(context, id + "F16", {"entities" : qUnion([Q0, Q1]), "radius" : 1.5 * mm, "tangentPropagation" : true, "allowEdgeOverflow" : false});
        }
        {
            var Q0;
            Q0=qCreatedBy(makeId("Top.planeOp"),FACE);
            var sketch = newSketch(context, id + "F17", { "sketchPlane" : qUnion([Q0])});
            skCircle(sketch, "E238", {"center": v(-28.03, 32.78) * mm, "radius": 2.5 * mm});
            skCircle(sketch, "E239", {"center": v(23.37, 32.78) * mm, "radius": 2.5 * mm});
            skCircle(sketch, "E240", {"center": v(23.37, -32.47) * mm, "radius": 2.5 * mm});
            skCircle(sketch, "E241", {"center": v(-28.03, -32.47) * mm, "radius": 2.5 * mm});
            skSolve(sketch);
        }
        {
            var Q0;
            Q0 = qSketchRegion(id + "F17", true);
            extrude(context, id + "F18", {"entities" : qUnion([Q0]), "operationType" : NewBodyOperationType.REMOVE, "oppositeDirection" : true, "depth" : 5 * mm, "hasSecondDirection" : true, "secondDirectionOppositeDirection" : true, "secondDirectionDepth" : 1 * mm});
        }
        {
            var Q0;
            Q0=qCreatedBy(id+"F1.planeOp",FACE);
            var sketch = newSketch(context, id + "F19", { "sketchPlane" : qUnion([Q0])});
            skCircle(sketch, "E242", {"center": v(-14.08, 41.18) * mm, "radius": 1.5 * mm});
            skCircle(sketch, "E243", {"center": v(9.42, 41.18) * mm, "radius": 1.5 * mm});
            skCircle(sketch, "E244", {"center": v(-14.08, 41.18) * mm, "radius": 2.5 * mm});
            skCircle(sketch, "E245", {"center": v(9.42, 41.18) * mm, "radius": 2.5 * mm});
            skSolve(sketch);
        }
        {
            var Q0;
            Q0=qCreatedBy(id+"F1.planeOp",FACE);
            var sketch = newSketch(context, id + "F20", { "sketchPlane" : qUnion([Q0])});
            skArc(sketch, "E246", {"start": v(-16.58, 41.18) * mm, "mid": v(-14.08, 38.68) * mm, "end": v(-11.58, 41.18) * mm});
            skArc(sketch, "E247", {"start": v(6.92, 41.18) * mm, "mid": v(9.42, 38.68) * mm, "end": v(11.92, 41.18) * mm});
            skLineSegment(sketch, "E248", {"start": v(-16.58, 41.18) * mm, "end": v(-16.58, 45.78) * mm});
            skLineSegment(sketch, "E249", {"start": v(-11.58, 41.18) * mm, "end": v(-11.58, 45.78) * mm});
            skLineSegment(sketch, "E250", {"start": v(-11.58, 45.78) * mm, "end": v(-16.58, 45.78) * mm});
            skLineSegment(sketch, "E251", {"start": v(6.92, 41.18) * mm, "end": v(6.92, 46.07) * mm});
            skLineSegment(sketch, "E252", {"start": v(11.92, 41.18) * mm, "end": v(11.92, 46.07) * mm});
            skLineSegment(sketch, "E253", {"start": v(11.92, 46.07) * mm, "end": v(6.92, 46.07) * mm});
            skSolve(sketch);
        }
        {
            var Q0;
            Q0=qCreatedBy(id+"F1.planeOp",FACE);
            var sketch = newSketch(context, id + "F21", { "sketchPlane" : qUnion([Q0])});
            skCircle(sketch, "E254", {"center": v(-14.08, 41.18) * mm, "radius": 2.5 * mm});
            skCircle(sketch, "E255", {"center": v(9.42, 41.18) * mm, "radius": 2.5 * mm});
            skSolve(sketch);
        }
        {
            var Q0;
            Q0 = qSketchRegion(id + "F21", true);
            extrude(context, id + "F22", {"entities" : qUnion([Q0]), "operationType" : NewBodyOperationType.REMOVE, "oppositeDirection" : true, "depth" : 3.2 * mm});
        }
    });
